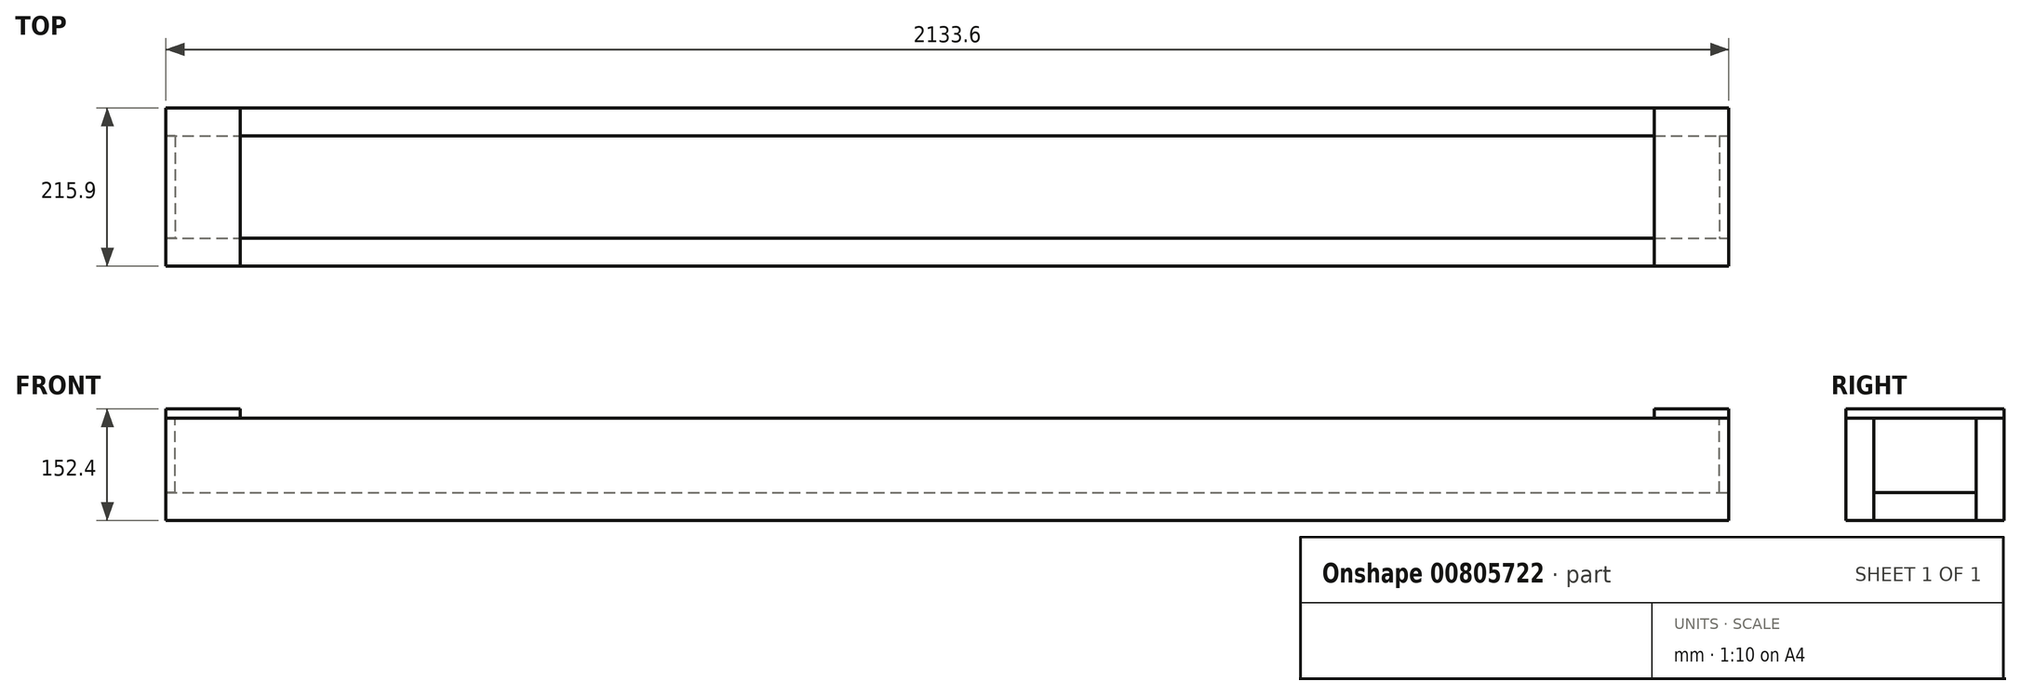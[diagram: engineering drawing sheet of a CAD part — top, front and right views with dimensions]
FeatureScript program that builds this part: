
annotation { "Feature Type Name" : "Feature", "Feature Type Description" : "" }
export const myFeature = defineFeature(function(context is Context, id is Id, definition is map)
    precondition{}
    {
        {
            var Q0;
            Q0=qCreatedBy(makeId("Top.planeOp"),FACE);
            var sketch = newSketch(context, id + "F0", { "sketchPlane" : qUnion([Q0])});
            skLineSegment(sketch, "E0.bottom", {"start": v(-1066.8, 69.85) * mm, "end": v(1066.8, 69.85) * mm});
            skLineSegment(sketch, "E0.top", {"start": v(-1066.8, -69.85) * mm, "end": v(1066.8, -69.85) * mm});
            skLineSegment(sketch, "E0.left", {"start": v(-1066.8, 69.85) * mm, "end": v(-1066.8, -69.85) * mm});
            skLineSegment(sketch, "E0.right", {"start": v(1066.8, 69.85) * mm, "end": v(1066.8, -69.85) * mm});
            skPoint(sketch, "E0.middle", {"position": v(0, 0) * mm});
            skSolve(sketch);
        }
        {
            var Q0;
            Q0=makeQuery(id+"F0.imprint","IMPRINT",FACE,{"disambiguationData":[TD([[makeQuery(id+"F0.imprint","IMPRINT",EDGE,{"derivedFrom":sQuery(id+"F0.wireOp",EDGE,"E0.bottom")}),-1.0]])]});
            extrude(context, id + "F1", {"entities" : qUnion([Q0]), "depth" : 38.1 * mm, "offsetDistance" : 25.4 * mm});
        }
        {
            var Q0;
            Q0=makeQuery(id+"F1.opExtrude","SWEPT_FACE",FACE,{"disambiguationData":[OSD([sQuery(id+"F0.wireOp",EDGE,"E0.right")])]});
            var sketch = newSketch(context, id + "F2", { "sketchPlane" : qUnion([Q0])});
            skLineSegment(sketch, "E1.bottom", {"start": v(69.85, 0) * mm, "end": v(107.95, 0) * mm});
            skLineSegment(sketch, "E1.top", {"start": v(69.85, 139.7) * mm, "end": v(107.95, 139.7) * mm});
            skLineSegment(sketch, "E1.left", {"start": v(69.85, 0) * mm, "end": v(69.85, 139.7) * mm});
            skLineSegment(sketch, "E1.right", {"start": v(107.95, 0) * mm, "end": v(107.95, 139.7) * mm});
            skLineSegment(sketch, "E2.bottom", {"start": v(-69.85, 0) * mm, "end": v(-107.95, 0) * mm});
            skLineSegment(sketch, "E2.top", {"start": v(-69.85, 139.7) * mm, "end": v(-107.95, 139.7) * mm});
            skLineSegment(sketch, "E2.left", {"start": v(-69.85, 0) * mm, "end": v(-69.85, 139.7) * mm});
            skLineSegment(sketch, "E2.right", {"start": v(-107.95, 0) * mm, "end": v(-107.95, 139.7) * mm});
            skSolve(sketch);
        }
        {
            var Q0;
            Q0 = qSketchRegion(id + "F2", true);
            var Q1;
            Q1=makeQuery(id+"F1.opExtrude","SWEPT_FACE",FACE,{"disambiguationData":[OSD([sQuery(id+"F0.wireOp",EDGE,"E0.left")])]});
            extrude(context, id + "F3", {"entities" : qUnion([Q0]), "endBound" : BoundingType.UP_TO_SURFACE, "oppositeDirection" : true, "depth" : 25.4 * mm, "endBoundEntityFace" : qUnion([Q1]), "offsetDistance" : 25.4 * mm});
        }
        {
            var Q0;
            Q0=makeQuery(id+"F3.opExtrude","CAP_FACE",FACE,{"disambiguationData":[OSD([sQuery(id+"F2.wireOp",EDGE,"E1.bottom"),sQuery(id+"F2.wireOp",EDGE,"E1.top"),sQuery(id+"F2.wireOp",EDGE,"E1.left"),sQuery(id+"F2.wireOp",EDGE,"E1.right")])],"isStart":true});
            var sketch = newSketch(context, id + "F4", { "sketchPlane" : qUnion([Q0])});
            skLineSegment(sketch, "E3.bottom", {"start": v(69.85, 139.7) * mm, "end": v(-69.85, 139.7) * mm});
            skLineSegment(sketch, "E3.top", {"start": v(69.85, 38.1) * mm, "end": v(-69.85, 38.1) * mm});
            skLineSegment(sketch, "E3.left", {"start": v(69.85, 139.7) * mm, "end": v(69.85, 38.1) * mm});
            skLineSegment(sketch, "E3.right", {"start": v(-69.85, 139.7) * mm, "end": v(-69.85, 38.1) * mm});
            skSolve(sketch);
        }
        {
            var Q0;
            Q0 = qSketchRegion(id + "F4", true);
            extrude(context, id + "F5", {"entities" : qUnion([Q0]), "oppositeDirection" : true, "depth" : 12.7 * mm, "offsetDistance" : 25.4 * mm});
        }
        {
            var Q0;
            Q0=makeQuery(id+"F3.opExtrude","SWEPT_FACE",FACE,{"disambiguationData":[OSD([sQuery(id+"F2.wireOp",EDGE,"E1.top")])]});
            var sketch = newSketch(context, id + "F6", { "sketchPlane" : qUnion([Q0])});
            skLineSegment(sketch, "E4.bottom", {"start": v(1066.8, 107.95) * mm, "end": v(965.2, 107.95) * mm});
            skLineSegment(sketch, "E4.top", {"start": v(1066.8, -107.95) * mm, "end": v(965.2, -107.95) * mm});
            skLineSegment(sketch, "E4.left", {"start": v(1066.8, 107.95) * mm, "end": v(1066.8, -107.95) * mm});
            skLineSegment(sketch, "E4.right", {"start": v(965.2, 107.95) * mm, "end": v(965.2, -107.95) * mm});
            skSolve(sketch);
        }
        {
            var Q0;
            Q0 = qSketchRegion(id + "F6", true);
            extrude(context, id + "F7", {"entities" : qUnion([Q0]), "depth" : 12.7 * mm, "offsetDistance" : 25.4 * mm});
        }
        {
            var Q0;
            Q0=makeQuery(id+"F7.opExtrude","SWEPT_BODY",BODY,{"disambiguationData":[OSD([sQuery(id+"F6.wireOp",EDGE,"E4.bottom"),sQuery(id+"F6.wireOp",EDGE,"E4.top"),sQuery(id+"F6.wireOp",EDGE,"E4.left"),sQuery(id+"F6.wireOp",EDGE,"E4.right")])]});
            var Q1;
            Q1=makeQuery(id+"F5.opExtrude","SWEPT_BODY",BODY,{"disambiguationData":[OSD([sQuery(id+"F4.wireOp",EDGE,"E3.bottom"),sQuery(id+"F4.wireOp",EDGE,"E3.top"),sQuery(id+"F4.wireOp",EDGE,"E3.left"),sQuery(id+"F4.wireOp",EDGE,"E3.right")])]});
            var Q2;
            Q2=qCreatedBy(makeId("Right.planeOp"),FACE);
            mirror(context, id + "F8", {"entities" : qUnion([Q0, Q1]), "mirrorPlane" : qUnion([Q2])});
        }
        {
            var Q0;
            Q0=qCreatedBy(makeId("Right.planeOp"),FACE);
            var sketch = newSketch(context, id + "F9", { "sketchPlane" : qUnion([Q0])});
            skLineSegment(sketch, "E5", {"start": v(-107.95, 152.4) * mm, "end": v(107.95, 0) * mm});
            skPoint(sketch, "E6", {"position": v(0, 76.2) * mm});
            skLineSegment(sketch, "E7", {"start": v(0, 76.2) * mm, "end": v(0, 123.04) * mm});
            skLineSegment(sketch, "E8", {"start": v(0, 76.2) * mm, "end": v(60.75, 76.2) * mm});
            skSolve(sketch);
        }
    });
